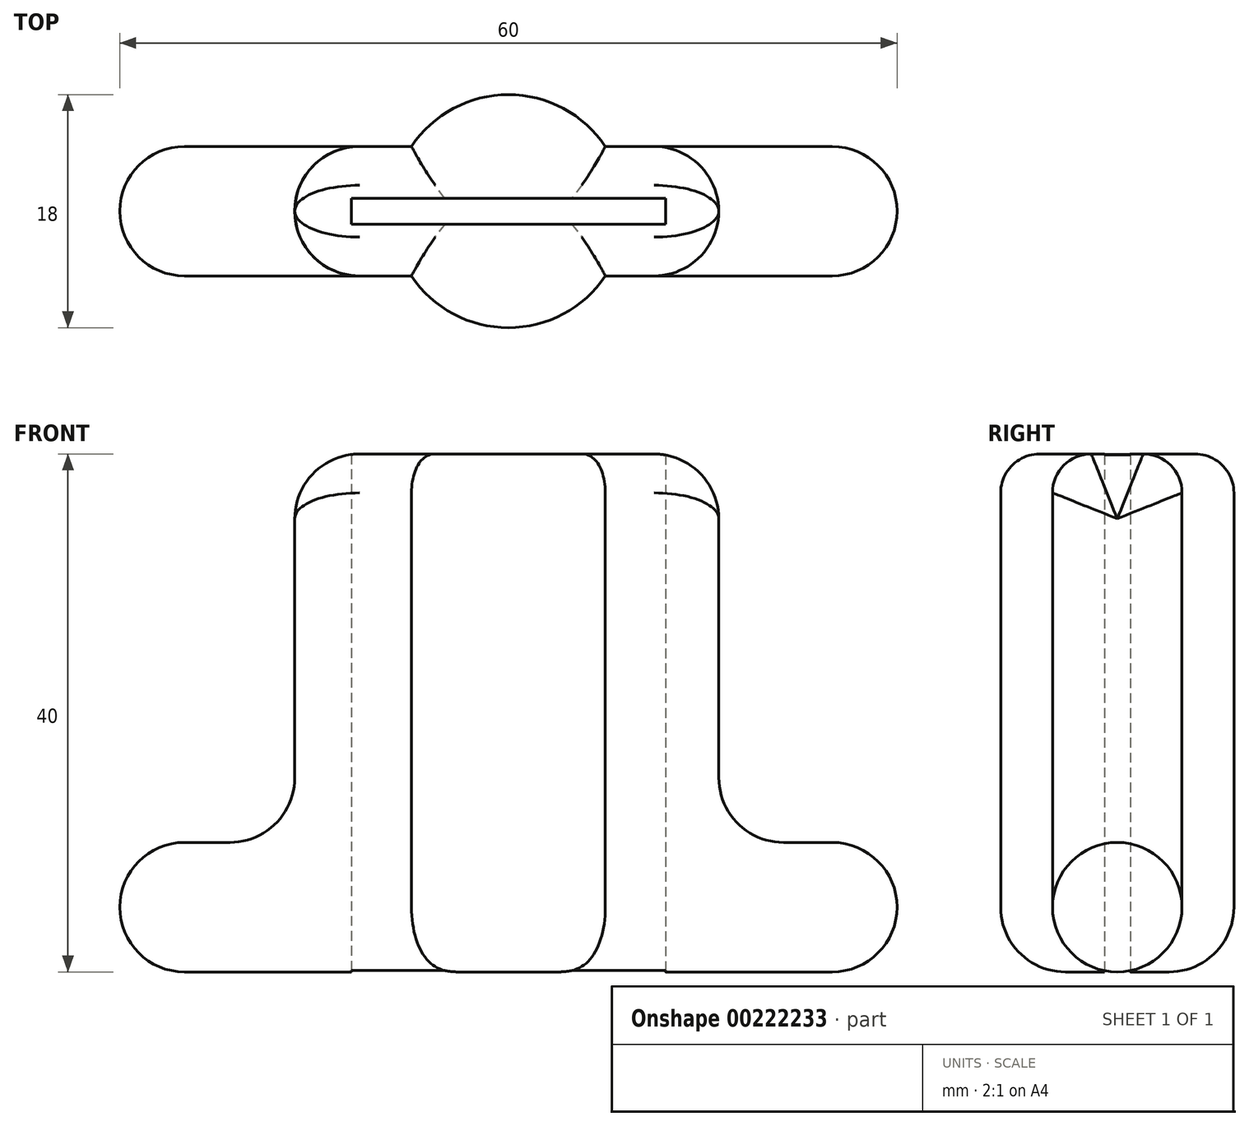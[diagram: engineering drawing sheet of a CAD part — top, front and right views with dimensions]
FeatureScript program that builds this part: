
annotation { "Feature Type Name" : "Feature", "Feature Type Description" : "" }
export const myFeature = defineFeature(function(context is Context, id is Id, definition is map)
    precondition{}
    {
        {
            var Q0;
            Q0=qCreatedBy(makeId("Top.planeOp"),FACE);
            var sketch = newSketch(context, id + "F0", { "sketchPlane" : qUnion([Q0])});
            skCircle(sketch, "E0", {"center": v(0, 0) * mm, "radius": 9 * mm});
            skPoint(sketch, "E1", {"position": v(-30, 0) * mm});
            skPoint(sketch, "E2", {"position": v(30, 0) * mm});
            skPoint(sketch, "E3", {"position": v(-30, 5) * mm});
            skPoint(sketch, "E4", {"position": v(30, 5) * mm});
            skPoint(sketch, "E5", {"position": v(30, -5) * mm});
            skPoint(sketch, "E6", {"position": v(-30, -5) * mm});
            skPoint(sketch, "E7", {"position": v(-7.48, 5) * mm});
            skPoint(sketch, "E8", {"position": v(-7.48, -5) * mm});
            skPoint(sketch, "E9", {"position": v(7.48, 5) * mm});
            skPoint(sketch, "E10", {"position": v(7.48, -5) * mm});
            skLineSegment(sketch, "E11", {"start": v(-25, 5) * mm, "end": v(-7.48, 5) * mm});
            skLineSegment(sketch, "E12", {"start": v(-29.85, -0.1) * mm, "end": v(-29.85, -0.1) * mm});
            skLineSegment(sketch, "E13", {"start": v(-25, -5) * mm, "end": v(-7.48, -5) * mm});
            skLineSegment(sketch, "E14", {"start": v(7.48, 5) * mm, "end": v(25, 5) * mm});
            skLineSegment(sketch, "E15", {"start": v(30.15, -0.1) * mm, "end": v(30.15, -0.1) * mm});
            skLineSegment(sketch, "E16", {"start": v(25, -5) * mm, "end": v(7.48, -5) * mm});
            skArc(sketch, "E17.filletArc", {"start": v(-25, 5) * mm, "mid": v(-28.54, 3.54) * mm, "end": v(-30, 0) * mm});
            skArc(sketch, "E18.filletArc", {"start": v(-30, 0) * mm, "mid": v(-28.54, -3.54) * mm, "end": v(-25, -5) * mm});
            skArc(sketch, "E19.filletArc", {"start": v(30, 0) * mm, "mid": v(28.54, 3.54) * mm, "end": v(25, 5) * mm});
            skArc(sketch, "E20.filletArc", {"start": v(25, -5) * mm, "mid": v(28.54, -3.54) * mm, "end": v(30, 0) * mm});
            skLineSegment(sketch, "E21", {"start": v(-30, 0) * mm, "end": v(30, 0) * mm, "construction": true});
            skLineSegment(sketch, "E22.bottom", {"start": v(-12.12, 1) * mm, "end": v(12.12, 1) * mm});
            skLineSegment(sketch, "E22.top", {"start": v(-12.12, -1) * mm, "end": v(12.12, -1) * mm});
            skLineSegment(sketch, "E22.left", {"start": v(-12.12, 1) * mm, "end": v(-12.12, -1) * mm});
            skLineSegment(sketch, "E22.right", {"start": v(12.12, 1) * mm, "end": v(12.12, -1) * mm});
            skCircle(sketch, "E23", {"center": v(0, 0) * mm, "radius": 17 * mm});
            skPoint(sketch, "E24", {"position": v(16.25, 5) * mm});
            skPoint(sketch, "E25", {"position": v(16.25, -5) * mm});
            skPoint(sketch, "E26", {"position": v(-16.25, -5) * mm});
            skPoint(sketch, "E27", {"position": v(-16.25, 5) * mm});
            skSolve(sketch);
        }
        {
            var Q0;
            {var subQ4=sQuery(id+"F0.wireOp",EDGE,"E19.filletArc");Q0=makeQuery(id+"F0.imprint","IMPRINT",FACE,{"disambiguationData":[TD([[makeQuery(id+"F0.imprint","IMPRINT",EDGE,{"derivedFrom":subQ4}),1.0]])]});}
            var Q1;
            {var subQ12=sQuery(id+"F0.wireOp",EDGE,"E22.right");Q1=makeQuery(id+"F0.imprint","IMPRINT",FACE,{"disambiguationData":[TD([[makeQuery(id+"F0.imprint","IMPRINT",EDGE,{"derivedFrom":subQ12}),1.0]])]});}
            var Q2;
            {var subQ8=sQuery(id+"F0.wireOp",EDGE,"E22.left");Q2=makeQuery(id+"F0.imprint","IMPRINT",FACE,{"disambiguationData":[TD([[makeQuery(id+"F0.imprint","IMPRINT",EDGE,{"derivedFrom":subQ8}),-1.0]])]});}
            var Q3;
            {var subQ1=sQuery(id+"F0.wireOp",EDGE,"E17.filletArc");Q3=makeQuery(id+"F0.imprint","IMPRINT",FACE,{"disambiguationData":[TD([[makeQuery(id+"F0.imprint","IMPRINT",EDGE,{"derivedFrom":subQ1}),1.0]])]});}
            var Q4;
            {var subQ0=sQuery(id+"F0.wireOp",EDGE,"E0");var subQ1=makeQuery(id+"F0.imprint","INTERSECT",VERTEX,{"derivedFrom":[subQ0,sQuery(id+"F0.wireOp",EDGE,"E14")]});Q4=makeQuery(id+"F0.imprint","IMPRINT",FACE,{"disambiguationData":[TD([[makeQuery(id+"F0.imprint","IMPRINT",EDGE,{"disambiguationData":[TD([[subQ1,1.0]])],"derivedFrom":subQ0}),1.0]])]});}
            var Q5;
            {var subQ0=sQuery(id+"F0.wireOp",EDGE,"E0");var subQ1=makeQuery(id+"F0.imprint","INTERSECT",VERTEX,{"derivedFrom":[subQ0,sQuery(id+"F0.wireOp",EDGE,"E13")]});Q5=makeQuery(id+"F0.imprint","IMPRINT",FACE,{"disambiguationData":[TD([[makeQuery(id+"F0.imprint","IMPRINT",EDGE,{"disambiguationData":[TD([[subQ1,1.0]])],"derivedFrom":subQ0}),1.0]])]});}
            extrude(context, id + "F1", {"entities" : qUnion([Q0, Q1, Q2, Q3, Q4, Q5]), "depth" : 40 * mm});
        }
        {
            var Q0;
            Q0=makeQuery(id+"F1.opExtrude","SWEPT_FACE",FACE,{"disambiguationData":[OSD([sQuery(id+"F0.wireOp",EDGE,"E16")])]});
            var sketch = newSketch(context, id + "F2", { "sketchPlane" : qUnion([Q0])});
            skPoint(sketch, "E28", {"position": v(16.24, 40) * mm});
            skPoint(sketch, "E29", {"position": v(0, 40) * mm});
            skPoint(sketch, "E30", {"position": v(-16.5, 40) * mm});
            skPoint(sketch, "E31", {"position": v(25, 10) * mm});
            skPoint(sketch, "E32", {"position": v(-24.99, 10) * mm});
            skPoint(sketch, "E33.third.point", {"position": v(-56.03, 0) * mm});
            skPoint(sketch, "E34.third.point", {"position": v(52.87, 0) * mm});
            skPoint(sketch, "E35", {"position": v(-16.5, 10) * mm});
            skPoint(sketch, "E36", {"position": v(16.24, 10) * mm});
            skLineSegment(sketch, "E37.bottom", {"start": v(-16.5, 10) * mm, "end": v(-34.5, 10) * mm});
            skLineSegment(sketch, "E37.top", {"start": v(-16.5, 40) * mm, "end": v(-34.5, 40) * mm});
            skLineSegment(sketch, "E37.left", {"start": v(-16.5, 10) * mm, "end": v(-16.5, 40) * mm});
            skLineSegment(sketch, "E37.right", {"start": v(-34.5, 10) * mm, "end": v(-34.5, 40) * mm});
            skLineSegment(sketch, "E38.bottom", {"start": v(16.24, 10) * mm, "end": v(34.24, 10) * mm});
            skLineSegment(sketch, "E38.top", {"start": v(16.24, 40) * mm, "end": v(34.24, 40) * mm});
            skLineSegment(sketch, "E38.left", {"start": v(16.24, 10) * mm, "end": v(16.24, 40) * mm});
            skLineSegment(sketch, "E38.right", {"start": v(34.24, 10) * mm, "end": v(34.24, 40) * mm});
            skSolve(sketch);
        }
        {
            var Q0;
            Q0 = qSketchRegion(id + "F2", true);
            extrude(context, id + "F3", {"entities" : qUnion([Q0]), "operationType" : NewBodyOperationType.REMOVE, "oppositeDirection" : true, "depth" : 25 * mm});
        }
        {
            var Q0;
            {var subQ2=sQuery(id+"F2.wireOp",EDGE,"E38.top");Q0=makeQuery(id+"F2.imprint","IMPRINT",FACE,{"disambiguationData":[TD([[makeQuery(id+"F2.imprint","IMPRINT",EDGE,{"derivedFrom":subQ2}),-1.0]])]});}
            var Q1;
            {var subQ0=sQuery(id+"F2.wireOp",EDGE,"E38.left");var subQ1=sQuery(id+"F2.wireOp",EDGE,"E38.bottom");var subQ2=makeQuery(id+"F2.imprint","INTERSECT",VERTEX,{"derivedFrom":[subQ1,subQ0]});Q1=makeQuery(id+"F2.imprint","IMPRINT",FACE,{"disambiguationData":[TD([[makeQuery(id+"F2.imprint","IMPRINT",EDGE,{"disambiguationData":[TD([[subQ2,-1.0]])],"derivedFrom":subQ0}),-1.0]])]});}
            var Q2;
            Q2=makeQuery(id+"F2.imprint","IMPRINT",FACE,{"disambiguationData":[TD([[makeQuery(id+"F2.imprint","IMPRINT",EDGE,{"derivedFrom":sQuery(id+"F2.wireOp",EDGE,"E37.bottom")}),-1.0]])]});
            extrude(context, id + "F4", {"entities" : qUnion([Q0, Q1, Q2]), "operationType" : NewBodyOperationType.REMOVE, "oppositeDirection" : true, "depth" : 10.8 * mm});
        }
        {
            var Q0;
            Q0=makeQuery(id+"F3.boolean.opBoolean","COPY",FACE,{"derivedFrom":makeQuery(id+"F3.opExtrude","SWEPT_FACE",FACE,{"disambiguationData":[OSD([sQuery(id+"F2.wireOp",EDGE,"E38.bottom")])]})});
            var Q1;
            Q1=makeQuery(id+"F3.boolean.opBoolean","COPY",FACE,{"derivedFrom":makeQuery(id+"F3.opExtrude","SWEPT_FACE",FACE,{"disambiguationData":[OSD([sQuery(id+"F2.wireOp",EDGE,"E37.bottom")])]})});
            var Q2;
            Q2=makeQuery(id+"F3.boolean.opBoolean","COPY",FACE,{"derivedFrom":makeQuery(id+"F3.opExtrude","SWEPT_FACE",FACE,{"disambiguationData":[OSD([sQuery(id+"F2.wireOp",EDGE,"E37.left")])]})});
            var Q3;
            Q3=makeQuery(id+"F3.boolean.opBoolean","COPY",FACE,{"derivedFrom":makeQuery(id+"F3.opExtrude","SWEPT_FACE",FACE,{"disambiguationData":[OSD([sQuery(id+"F2.wireOp",EDGE,"E38.left")])]})});
            fillet(context, id + "F5", {"entities" : qUnion([Q0, Q1, Q2, Q3]), "radius" : 5 * mm, "tangentPropagation" : true, "allowEdgeOverflow" : false});
        }
        {
            var Q0;
            Q0=makeQuery(id+"F1.opExtrude","CAP_EDGE",EDGE,{"disambiguationData":[OSD([sQuery(id+"F0.wireOp",EDGE,"E14")])],"isStart":true});
            var Q1;
            Q1=makeQuery(id+"F1.opExtrude","CAP_EDGE",EDGE,{"disambiguationData":[OSD([sQuery(id+"F0.wireOp",EDGE,"E19.filletArc"),sQuery(id+"F0.wireOp",EDGE,"E20.filletArc")])],"isStart":true});
            var Q2;
            Q2=makeQuery(id+"F1.opExtrude","CAP_EDGE",EDGE,{"disambiguationData":[OSD([sQuery(id+"F0.wireOp",EDGE,"E16")])],"isStart":true});
            var Q3;
            {var subQ0=sQuery(id+"F0.wireOp",EDGE,"E0");Q3=makeQuery(id+"F1.opExtrude","CAP_EDGE",EDGE,{"disambiguationData":[OSD([subQ0]),TDD([makeQuery(id+"F0.imprint","IMPRINT",EDGE,{"disambiguationData":[TD([[makeQuery(id+"F0.imprint","INTERSECT",VERTEX,{"derivedFrom":[subQ0,sQuery(id+"F0.wireOp",EDGE,"E13")]}),-1.0]])],"derivedFrom":subQ0})])],"isStart":true});}
            var Q4;
            Q4=makeQuery(id+"F1.opExtrude","CAP_EDGE",EDGE,{"disambiguationData":[OSD([sQuery(id+"F0.wireOp",EDGE,"E13")])],"isStart":true});
            var Q5;
            Q5=makeQuery(id+"F1.opExtrude","CAP_EDGE",EDGE,{"disambiguationData":[OSD([sQuery(id+"F0.wireOp",EDGE,"E17.filletArc"),sQuery(id+"F0.wireOp",EDGE,"E18.filletArc")])],"isStart":true});
            var Q6;
            Q6=makeQuery(id+"F1.opExtrude","CAP_EDGE",EDGE,{"disambiguationData":[OSD([sQuery(id+"F0.wireOp",EDGE,"E11")])],"isStart":true});
            var Q7;
            {var subQ0=sQuery(id+"F0.wireOp",EDGE,"E0");Q7=makeQuery(id+"F1.opExtrude","CAP_EDGE",EDGE,{"disambiguationData":[OSD([subQ0]),TDD([makeQuery(id+"F0.imprint","IMPRINT",EDGE,{"disambiguationData":[TD([[makeQuery(id+"F0.imprint","INTERSECT",VERTEX,{"derivedFrom":[subQ0,sQuery(id+"F0.wireOp",EDGE,"E11")]}),1.0]])],"derivedFrom":subQ0})])],"isStart":true});}
            fillet(context, id + "F6", {"entities" : qUnion([Q0, Q1, Q2, Q3, Q4, Q5, Q6, Q7]), "radius" : 5 * mm, "tangentPropagation" : true, "allowEdgeOverflow" : false});
        }
        {
            var Q0;
            {var subQ0=sQuery(id+"F0.wireOp",EDGE,"E0");Q0=makeQuery(id+"F1.opExtrude","CAP_EDGE",EDGE,{"disambiguationData":[OSD([subQ0]),TDD([makeQuery(id+"F0.imprint","IMPRINT",EDGE,{"disambiguationData":[TD([[makeQuery(id+"F0.imprint","INTERSECT",VERTEX,{"derivedFrom":[subQ0,sQuery(id+"F0.wireOp",EDGE,"E11")]}),1.0]])],"derivedFrom":subQ0})])],"isStart":false});}
            var Q1;
            {var subQ0=sQuery(id+"F2.wireOp",EDGE,"E38.left");Q1=makeQuery(id+"F5.opFillet","BLEND_EDGE",EDGE,{"blendedFrom":[makeQuery(id+"F3.boolean.opBoolean","COPY",EDGE,{"derivedFrom":makeQuery(id+"F3.opExtrude","SWEPT_EDGE",EDGE,{"disambiguationData":[OSD([sQuery(id+"F0.wireOp",EDGE,"E16"),sQuery(id+"F2.wireOp",EDGE,"E38.top"),subQ0])]})}),makeQuery(id+"F3.boolean.opBoolean","INTERSECT",EDGE,{"derivedFrom":[makeQuery(id+"F1.opExtrude","SWEPT_FACE",FACE,{"disambiguationData":[OSD([sQuery(id+"F0.wireOp",EDGE,"E14")])]}),makeQuery(id+"F3.opExtrude","SWEPT_FACE",FACE,{"disambiguationData":[OSD([subQ0])]})]})],"blendedInto":[]});}
            var Q2;
            Q2=makeQuery(id+"F1.opExtrude","CAP_EDGE",EDGE,{"disambiguationData":[OSD([sQuery(id+"F0.wireOp",EDGE,"E14")])],"isStart":false});
            var Q3;
            {var subQ0=sQuery(id+"F2.wireOp",EDGE,"E38.left");Q3=makeQuery(id+"F5.opFillet","BLEND_EDGE",EDGE,{"blendedFrom":[makeQuery(id+"F3.boolean.opBoolean","COPY",EDGE,{"derivedFrom":makeQuery(id+"F3.opExtrude","SWEPT_EDGE",EDGE,{"disambiguationData":[OSD([sQuery(id+"F0.wireOp",EDGE,"E16"),sQuery(id+"F2.wireOp",EDGE,"E38.top"),subQ0])]})}),makeQuery(id+"F3.boolean.opBoolean","COPY",EDGE,{"derivedFrom":makeQuery(id+"F3.opExtrude","CAP_EDGE",EDGE,{"disambiguationData":[OSD([subQ0])],"isStart":true})})],"blendedInto":[]});}
            var Q4;
            Q4=makeQuery(id+"F1.opExtrude","CAP_EDGE",EDGE,{"disambiguationData":[OSD([sQuery(id+"F0.wireOp",EDGE,"E16")])],"isStart":false});
            var Q5;
            {var subQ0=sQuery(id+"F0.wireOp",EDGE,"E0");Q5=makeQuery(id+"F1.opExtrude","CAP_EDGE",EDGE,{"disambiguationData":[OSD([subQ0]),TDD([makeQuery(id+"F0.imprint","IMPRINT",EDGE,{"disambiguationData":[TD([[makeQuery(id+"F0.imprint","INTERSECT",VERTEX,{"derivedFrom":[subQ0,sQuery(id+"F0.wireOp",EDGE,"E13")]}),-1.0]])],"derivedFrom":subQ0})])],"isStart":false});}
            var Q6;
            Q6=makeQuery(id+"F1.opExtrude","CAP_EDGE",EDGE,{"disambiguationData":[OSD([sQuery(id+"F0.wireOp",EDGE,"E11")])],"isStart":false});
            var Q7;
            {var subQ0=sQuery(id+"F2.wireOp",EDGE,"E37.left");Q7=makeQuery(id+"F5.opFillet","BLEND_EDGE",EDGE,{"blendedFrom":[makeQuery(id+"F3.boolean.opBoolean","COPY",EDGE,{"derivedFrom":makeQuery(id+"F3.opExtrude","SWEPT_EDGE",EDGE,{"disambiguationData":[OSD([sQuery(id+"F2.wireOp",EDGE,"E37.top"),subQ0])]})}),makeQuery(id+"F3.boolean.opBoolean","INTERSECT",EDGE,{"derivedFrom":[makeQuery(id+"F1.opExtrude","SWEPT_FACE",FACE,{"disambiguationData":[OSD([sQuery(id+"F0.wireOp",EDGE,"E11")])]}),makeQuery(id+"F3.opExtrude","SWEPT_FACE",FACE,{"disambiguationData":[OSD([subQ0])]})]})],"blendedInto":[]});}
            var Q8;
            {var subQ0=sQuery(id+"F2.wireOp",EDGE,"E37.left");Q8=makeQuery(id+"F5.opFillet","BLEND_EDGE",EDGE,{"blendedFrom":[makeQuery(id+"F3.boolean.opBoolean","COPY",EDGE,{"derivedFrom":makeQuery(id+"F3.opExtrude","SWEPT_EDGE",EDGE,{"disambiguationData":[OSD([sQuery(id+"F2.wireOp",EDGE,"E37.top"),subQ0])]})}),makeQuery(id+"F3.boolean.opBoolean","COPY",EDGE,{"derivedFrom":makeQuery(id+"F3.opExtrude","CAP_EDGE",EDGE,{"disambiguationData":[OSD([subQ0])],"isStart":true})})],"blendedInto":[]});}
            var Q9;
            Q9=makeQuery(id+"F1.opExtrude","CAP_EDGE",EDGE,{"disambiguationData":[OSD([sQuery(id+"F0.wireOp",EDGE,"E13")])],"isStart":false});
            fillet(context, id + "F7", {"entities" : qUnion([Q0, Q1, Q2, Q3, Q4, Q5, Q6, Q7, Q8, Q9]), "radius" : 3 * mm, "tangentPropagation" : true, "allowEdgeOverflow" : false});
        }
    });
